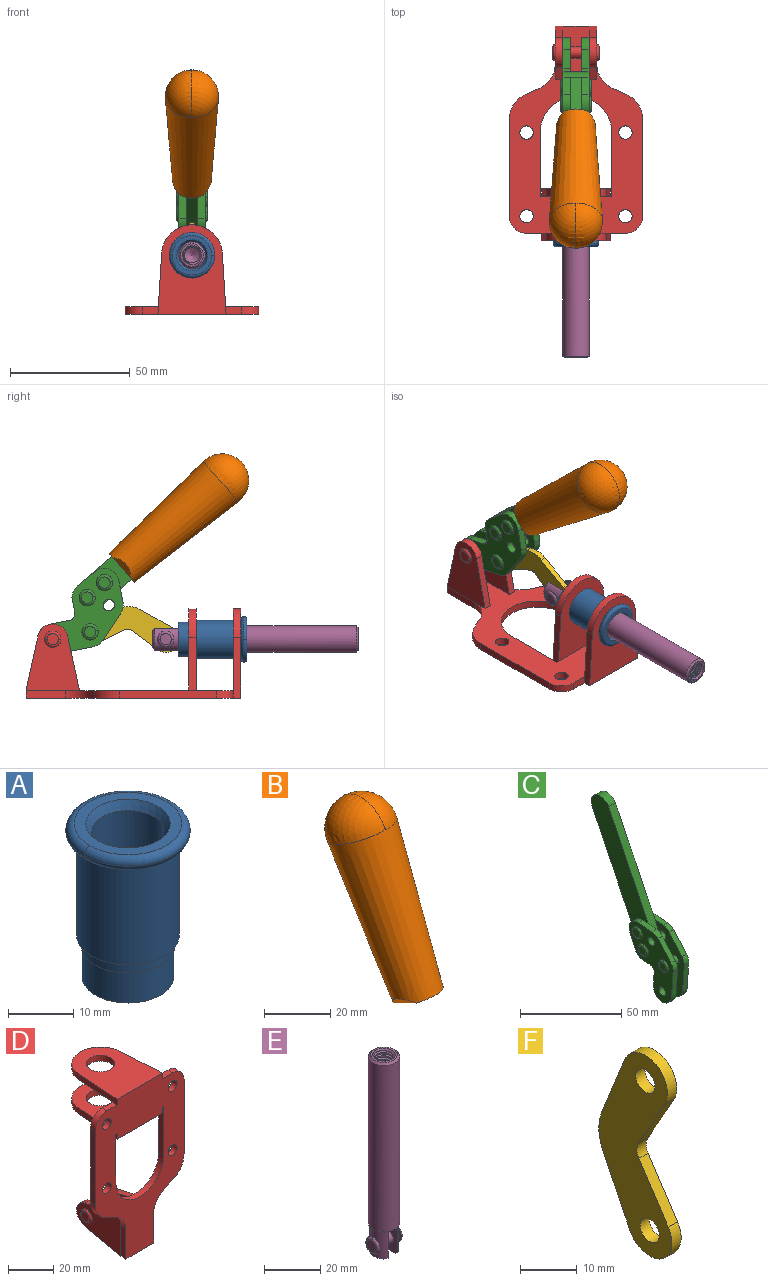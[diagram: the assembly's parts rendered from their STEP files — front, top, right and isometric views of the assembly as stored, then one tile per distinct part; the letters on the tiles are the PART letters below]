
ASSEMBLY  parts=6 mates=6
PART A: 15 faces, bbox 20.6x20.6x28.7 mm
  f0: torus R=8.26mm, axis (0,0,1), area 56.8mm2, adj f1,f10,f12
  f1: torus R=8.26mm, axis (0,0,1), area 56.8mm2, adj f0,f6,f13
  f2: cylinder r=5.59mm len=25.91mm, axis (0,0,1), area 909.6mm2, adj f3,f4
  f3: cone r=6.86mm half-angle=45deg, axis (0,0,-1), area 70.2mm2, adj f2,f14
  f4: cone r=6.47mm half-angle=30deg, axis (0,0,1), area 66.7mm2, adj f2,f13
  f5: cylinder r=7.04mm len=14.07mm, axis (0,0,1), area 252.6mm2, adj f11,f14
  f6: torus R=8.26mm, axis (0,0,1), area 56.8mm2, adj f1,f12,f13
  f7: cylinder r=7.16mm len=14.33mm, axis (0,0,1), area 91.5mm2, adj f9,f11
  f8: cylinder r=7.86mm len=18.42mm, axis (0,0,1), area 909.6mm2, adj f9,f10
  f9: plane 15.72x15.72mm, normal (0,0,-1), area 33mm2, adj f7,f8
  f10: plane 16.51x16.51mm, normal (0,0,-1), area 19.9mm2, adj f0,f8,f12
  f11: plane 14.33x14.33mm, normal (0,0,-1), area 5.7mm2, adj f5,f7
  f12: torus R=8.26mm, axis (0,0,1), area 56.8mm2, adj f0,f6,f10
  f13: plane 16.51x16.51mm, normal (0,0,1), area 82.7mm2, adj f1,f4,f6
  f14: plane 14.07x14.07mm, normal (0,0,-1), area 7.8mm2, adj f3,f5
PART B: 11 faces, bbox 22.3x42.6x64.5 mm
  f0: sphere r=11.13mm, area 411.4mm2, adj f1,f8
  f1: cone r=11.11mm half-angle=3.3deg, axis (0,0.44,0.9), area 3251.8mm2, adj f0,f7,f8,f9,f10
  f2: cylinder r=6.16mm len=11.7mm, axis (1,0,0), area 89.5mm2, adj f3,f4,f5,f6
  f3: plane 60.23x36.75mm, normal (-1,0,0), area 763.6mm2, adj f2,f4,f6,f10
  f4: plane 51.37x25.05mm, normal (0,0.9,-0.44), area 264.2mm2, adj f2,f3,f5,f10
  f5: plane 60.23x36.75mm, normal (1,0,0), area 763.6mm2, adj f2,f4,f6,f10
  f6: plane 51.37x25.05mm, normal (0,-0.9,0.44), area 264.2mm2, adj f2,f3,f5,f10
  f7: plane 9.95x5.95mm, normal (0.71,-0.31,-0.64), area 25.8mm2, adj f1,f10
  f8: sphere r=11.13mm, area 411.4mm2, adj f0,f1
  f9: plane 9.95x5.95mm, normal (-0.71,-0.31,-0.64), area 25.8mm2, adj f1,f10
  f10: plane 14.27x11.38mm, normal (0,-0.44,-0.9), area 106.7mm2, adj f1,f3,f4,f5,f6,f7,f9
PART C: 59 faces, bbox 12.9x60.2x99.6 mm
  f0: torus R=2.39mm, axis (-1,0,0), area 14.9mm2, adj f20,f43,f51
  f1: torus R=2.39mm, axis (-1,0,0), area 14.9mm2, adj f19,f42,f51
  f2: torus R=2.39mm, axis (-1,0,0), area 14.9mm2, adj f18,f35,f51
  f3: torus R=2.39mm, axis (-1,0,0), area 14.9mm2, adj f14,f17,f23
  f4: torus R=2.39mm, axis (-1,0,0), area 14.9mm2, adj f13,f16,f23
  f5: torus R=2.39mm, axis (-1,0,0), area 14.9mm2, adj f12,f15,f23
  f6: cylinder r=2.39mm len=4.78mm, axis (1,0,0), area 46.5mm2, adj f48,f50,f51
  f7: cylinder r=2.39mm len=4.78mm, axis (1,0,0), area 46.5mm2, adj f50,f51
  f8: cylinder r=6.35mm len=12.68mm, axis (1,0,0), area 61.8mm2, adj f38,f39,f50,f51
  f9: cylinder r=2.39mm len=4.78mm, axis (-1,0,0), area 70.5mm2, adj f46,f50
  f10: cylinder r=2.39mm len=4.78mm, axis (-1,0,0), area 46.5mm2, adj f23,f45,f46
  f11: cylinder r=2.39mm len=4.78mm, axis (-1,0,0), area 46.5mm2, adj f23,f46
  f12: plane 4.78x4.78mm, normal (1,0,0), area 17.9mm2, adj f5,f15
  f13: plane 4.78x4.78mm, normal (1,0,0), area 17.9mm2, adj f4,f16
  f14: plane 4.78x4.78mm, normal (1,0,0), area 17.9mm2, adj f3,f17
  f15: torus R=2.39mm, axis (-1,0,0), area 14.9mm2, adj f5,f12,f23
  f16: torus R=2.39mm, axis (-1,0,0), area 14.9mm2, adj f4,f13,f23
  f17: torus R=2.39mm, axis (-1,0,0), area 14.9mm2, adj f3,f14,f23
  f18: plane 4.78x4.78mm, normal (-1,0,0), area 17.9mm2, adj f2,f35
  f19: plane 4.78x4.78mm, normal (-1,0,0), area 17.9mm2, adj f1,f42
  f20: plane 4.78x4.78mm, normal (-1,0,0), area 17.9mm2, adj f0,f43
  f21: plane 2.26x0.2mm, normal (1,0,0), area 0.2mm2, adj f31,f44
  f22: plane 2.26x0.2mm, normal (-1,0,0), area 0.2mm2, adj f41,f44
  f23: plane 39.37x30.77mm, normal (1,0,0), area 565.5mm2, adj f3,f4,f5,f10,f11,f15,f16,f17
  f24: cylinder r=6.1mm len=4.15mm, axis (-1,0,0), area 14.7mm2, adj f23,f25,f32,f46
  f25: plane 10.25x9.01mm, normal (0,-0.75,0.66), area 42.3mm2, adj f23,f24,f26,f46
  f26: cylinder r=6.35mm len=4.64mm, axis (-1,0,0), area 15.6mm2, adj f23,f25,f27,f46
  f27: plane 15.84x3.1mm, normal (0,-1,-0.07), area 49.2mm2, adj f23,f26,f28,f46
  f28: cylinder r=6.35mm len=12.68mm, axis (-1,0,0), area 61.8mm2, adj f23,f27,f29,f46
  f29: plane 8.11x3.1mm, normal (0,1,0.07), area 25.2mm2, adj f23,f28,f30,f46
  f30: cylinder r=3.05mm len=3.25mm, axis (-1,0,0), area 14.8mm2, adj f23,f29,f31,f46
  f31: plane 5.99x3.1mm, normal (0,0.07,-1), area 18.6mm2, adj f21,f23,f30,f44,f46
  f32: plane 9.5x3.1mm, normal (0,-0.07,1), area 29.5mm2, adj f23,f24,f33,f46,f47
  f33: cylinder r=6.1mm len=8.63mm, axis (-1,0,0), area 39.1mm2, adj f23,f32,f34,f47
  f34: plane 8.65x3.96mm, normal (0,0.91,-0.42), area 29.5mm2, adj f23,f33,f44,f47
  f35: torus R=2.39mm, axis (-1,0,0), area 14.9mm2, adj f2,f18,f51
  f36: plane 10.25x9.01mm, normal (0,-0.75,0.66), area 42.3mm2, adj f37,f49,f50,f51
  f37: cylinder r=6.35mm len=4.64mm, axis (1,0,0), area 15.6mm2, adj f36,f38,f50,f51
  f38: plane 15.84x3.1mm, normal (0,-1,-0.07), area 49.2mm2, adj f8,f37,f50,f51
  f39: plane 8.11x3.1mm, normal (0,1,0.07), area 25.2mm2, adj f8,f40,f50,f51
  f40: cylinder r=3.05mm len=3.25mm, axis (1,0,0), area 14.8mm2, adj f39,f41,f50,f51
  f41: plane 5.99x3.1mm, normal (0,0.07,-1), area 18.6mm2, adj f22,f40,f44,f50,f51
  f42: torus R=2.39mm, axis (-1,0,0), area 14.9mm2, adj f1,f19,f51
  f43: torus R=2.39mm, axis (-1,0,0), area 14.9mm2, adj f0,f20,f51
  f44: cylinder r=6.35mm len=12.12mm, axis (-1,0,0), area 128.9mm2, adj f21,f22,f23,f31,f34,f41,f46,f47
  f45: plane 2.65x1.35mm, normal (1,0,0), area 1mm2, adj f10,f55
  f46: plane 39.08x20.42mm, normal (-1,0,0), area 412.5mm2, adj f9,f10,f11,f24,f25,f26,f27,f28
  f47: plane 77.62x39.82mm, normal (1,0,0), area 850mm2, adj f32,f33,f34,f44,f53,f54,f55
  f48: plane 2.65x1.35mm, normal (-1,0,0), area 1mm2, adj f6,f55
  f49: cylinder r=6.1mm len=4.15mm, axis (1,0,0), area 14.7mm2, adj f36,f50,f51,f56
  f50: plane 39.08x20.42mm, normal (1,0,0), area 412.5mm2, adj f6,f7,f8,f9,f36,f37,f38,f39
  f51: plane 39.37x30.77mm, normal (-1,0,0), area 565.5mm2, adj f0,f1,f2,f6,f7,f8,f35,f36
  f52: plane 8.65x3.96mm, normal (0,0.91,-0.42), area 29.5mm2, adj f44,f51,f57,f58
  f53: plane 68.49x33.4mm, normal (0,0.9,-0.44), area 358.1mm2, adj f44,f47,f54,f58
  f54: cylinder r=6.35mm len=12.06mm, axis (1,0,0), area 93.7mm2, adj f47,f53,f55,f58
  f55: plane 68.49x33.4mm, normal (0,-0.9,0.44), area 358.1mm2, adj f44,f45,f46,f47,f48,f50,f54,f58
  f56: plane 9.5x3.1mm, normal (0,-0.07,1), area 29.5mm2, adj f49,f50,f51,f57,f58
  f57: cylinder r=6.1mm len=8.63mm, axis (1,0,0), area 39.1mm2, adj f51,f52,f56,f58
  f58: plane 77.62x39.82mm, normal (-1,0,0), area 850mm2, adj f44,f52,f53,f54,f55,f56,f57
PART D: 55 faces, bbox 55.7x37.4x89.8 mm
  f0: torus R=2.41mm, axis (-1,0,0), area 15mm2, adj f11,f15,f25
  f1: torus R=2.41mm, axis (-1,0,0), area 15mm2, adj f10,f12,f22
  f2: cylinder r=2.78mm len=5.56mm, axis (0,-1,0), area 54.2mm2, adj f30,f54
  f3: cylinder r=14.99mm len=29.97mm, axis (0,-1,0), area 145.9mm2, adj f30,f49,f53,f54
  f4: cylinder r=2.78mm len=5.56mm, axis (0,-1,0), area 54.2mm2, adj f30,f54
  f5: cylinder r=2.78mm len=5.56mm, axis (0,-1,0), area 54.2mm2, adj f30,f54
  f6: cylinder r=2.78mm len=5.56mm, axis (0,-1,0), area 54.2mm2, adj f30,f54
  f7: cylinder r=6.35mm len=12.7mm, axis (0,0,1), area 123.6mm2, adj f27,f51
  f8: cylinder r=6.35mm len=12.7mm, axis (0,0,-1), area 124.7mm2, adj f21,f35
  f9: cylinder r=2.41mm len=11.18mm, axis (-1,0,0), area 169.4mm2, adj f16,f19
  f10: plane 4.83x4.83mm, normal (1,0,0), area 18.3mm2, adj f1,f12
  f11: plane 4.83x4.83mm, normal (-1,0,0), area 18.3mm2, adj f0,f15
  f12: torus R=2.41mm, axis (-1,0,0), area 15mm2, adj f1,f10,f22
  f13: cylinder r=6.35mm len=12.41mm, axis (1,0,0), area 53.4mm2, adj f18,f19,f22,f23
  f14: cylinder r=6.35mm len=12.41mm, axis (-1,0,0), area 53.4mm2, adj f16,f17,f24,f25
  f15: torus R=2.41mm, axis (-1,0,0), area 15mm2, adj f0,f11,f25
  f16: plane 27.86x22.35mm, normal (1,0,0), area 425.4mm2, adj f9,f14,f17,f24,f30
  f17: plane 22.86x4.97mm, normal (0,0.21,0.98), area 72.5mm2, adj f14,f16,f25,f30
  f18: plane 22.86x4.97mm, normal (0,0.21,0.98), area 72.5mm2, adj f13,f19,f22,f30
  f19: plane 27.86x22.35mm, normal (-1,0,0), area 425.4mm2, adj f9,f13,f18,f23,f30
  f20: cylinder r=12.7mm len=25.35mm, axis (0,0,-1), area 119.8mm2, adj f21,f34,f35,f36
  f21: plane 34.21x28.07mm, normal (0,0,-1), area 702.4mm2, adj f8,f20,f30,f34,f36
  f22: plane 27.96x22.45mm, normal (1,0,0), area 407.2mm2, adj f1,f12,f13,f18,f23,f30,f42,f43
  f23: plane 22.86x4.97mm, normal (0,0.21,-0.98), area 72.5mm2, adj f13,f19,f22,f44
  f24: plane 22.86x4.97mm, normal (0,0.21,-0.98), area 72.5mm2, adj f14,f16,f25,f44
  f25: plane 27.86x22.35mm, normal (-1,0,0), area 407.1mm2, adj f0,f14,f15,f17,f24,f30,f45,f46
  f26: plane 3.1x0.95mm, normal (0,0,-1), area 2.7mm2, adj f30,f49,f50,f54
  f27: plane 34.21x28.07mm, normal (0,0,1), area 702.4mm2, adj f7,f28,f30,f50,f52
  f28: cylinder r=12.7mm len=25.35mm, axis (0,0,1), area 118.8mm2, adj f27,f50,f51,f52
  f29: plane 3.1x0.95mm, normal (0,0,-1), area 2.7mm2, adj f30,f52,f53,f54
  f30: plane 86.54x55.63mm, normal (0,1,0), area 2362.9mm2, adj f2,f3,f4,f5,f6,f16,f17,f18
  f31: plane 40.56x3.1mm, normal (-1,0,0), area 125.7mm2, adj f30,f32,f48,f54
  f32: cylinder r=7.11mm len=7.11mm, axis (0,-1,0), area 34.6mm2, adj f30,f31,f33,f54
  f33: plane 6.67x3.1mm, normal (0,0,1), area 20.4mm2, adj f30,f32,f34,f54
  f34: plane 25.39x3.13mm, normal (-1,0.06,0), area 79.5mm2, adj f20,f21,f33,f35,f54
  f35: plane 37.31x28.45mm, normal (0,0,1), area 789.9mm2, adj f8,f20,f34,f36,f54
  f36: plane 25.39x3.13mm, normal (1,0.06,0), area 79.5mm2, adj f20,f21,f35,f37,f54
  f37: plane 6.67x3.1mm, normal (0,0,1), area 20.4mm2, adj f30,f36,f38,f54
  f38: cylinder r=7.11mm len=7.11mm, axis (0,-1,0), area 34.6mm2, adj f30,f37,f39,f54
  f39: plane 40.56x3.1mm, normal (1,0,0), area 125.7mm2, adj f30,f38,f40,f54
  f40: cylinder r=11.18mm len=10.16mm, axis (0,-1,0), area 39.5mm2, adj f30,f39,f41,f54
  f41: plane 6.09x3.1mm, normal (0.42,0,-0.91), area 20.8mm2, adj f30,f40,f42,f54
  f42: cylinder r=11.18mm len=9.41mm, axis (0,-1,0), area 37.2mm2, adj f22,f30,f41,f43,f54
  f43: plane 16.5x3.1mm, normal (1,0,0), area 51.1mm2, adj f22,f42,f44,f54
  f44: plane 17.37x3.1mm, normal (0,0,-1), area 53.8mm2, adj f23,f24,f30,f43,f45,f54
  f45: plane 16.5x3.1mm, normal (-1,0,0), area 51.1mm2, adj f25,f44,f46,f54
  f46: cylinder r=11.18mm len=9.41mm, axis (0,-1,0), area 37.2mm2, adj f25,f30,f45,f47,f54
  f47: plane 6.09x3.1mm, normal (-0.42,0,-0.91), area 20.8mm2, adj f30,f46,f48,f54
  f48: cylinder r=11.18mm len=10.16mm, axis (0,-1,0), area 39.5mm2, adj f30,f31,f47,f54
  f49: plane 26.54x3.1mm, normal (-1,0,0), area 82.3mm2, adj f3,f26,f30,f54
  f50: plane 25.39x3.1mm, normal (1,0.06,0), area 78.8mm2, adj f26,f27,f28,f51,f54
  f51: plane 37.31x28.45mm, normal (0,0,-1), area 789.9mm2, adj f7,f28,f50,f52,f54
  f52: plane 25.39x3.1mm, normal (-1,0.06,0), area 78.8mm2, adj f27,f28,f29,f51,f54
  f53: plane 26.54x3.1mm, normal (1,0,0), area 82.3mm2, adj f3,f29,f30,f54
  f54: plane 89.66x55.63mm, normal (0,-1,0), area 2678.5mm2, adj f2,f3,f4,f5,f6,f26,f29,f31
PART E: 48 faces, bbox 12.6x11.1x86.1 mm
  f0: torus R=2.41mm, axis (-1,0,0), area 15mm2, adj f30,f32,f34
  f1: torus R=2.41mm, axis (-1,0,0), area 15mm2, adj f29,f31,f33
  f2: cylinder r=5.54mm len=72.39mm, axis (0,0,1), area 2518.5mm2, adj f3,f4,f42,f43
  f3: cone r=5.54mm half-angle=45deg, axis (0,0,1), area 7.6mm2, adj f2,f5,f41
  f4: cone r=5.54mm half-angle=45deg, axis (0,0,-1), area 34.9mm2, adj f2,f39
  f5: cylinder r=5.08mm len=11.48mm, axis (0,0,1), area 108.3mm2, adj f3,f7,f8,f41
  f6: cylinder r=2.41mm len=4.83mm, axis (-1,0,0), area 71.2mm2, adj f40,f41
  f7: cylinder r=2.41mm len=4.83mm, axis (-1,0,0), area 7.6mm2, adj f5,f34
  f8: cone r=5.08mm half-angle=45deg, axis (0,0,1), area 10.6mm2, adj f5,f37,f41
  f9: cone r=3.98mm half-angle=45deg, axis (0,0,1), area 17.6mm2, adj f27,f39,f45,f46,f47
  f10: cylinder r=2.41mm len=4.83mm, axis (-1,0,0), area 7.6mm2, adj f33,f38
  f11: cylinder r=3.2mm len=6.4mm, axis (0,0,1), area 78.4mm2, adj f12,f28,f44,f45,f47
  f12: cylinder r=3.2mm len=6.4mm, axis (0,0,1), area 10.5mm2, adj f11,f13,f45,f47
  f13: cylinder r=3.2mm len=6.4mm, axis (0,0,1), area 10.5mm2, adj f12,f14,f45,f47
  f14: cylinder r=3.2mm len=6.4mm, axis (0,0,1), area 10.5mm2, adj f13,f15,f45,f47
  f15: cylinder r=3.2mm len=6.4mm, axis (0,0,1), area 10.5mm2, adj f14,f16,f45,f47
  f16: cylinder r=3.2mm len=6.4mm, axis (0,0,1), area 10.5mm2, adj f15,f17,f45,f47
  f17: cylinder r=3.2mm len=6.4mm, axis (0,0,1), area 10.5mm2, adj f16,f18,f45,f47
  f18: cylinder r=3.2mm len=6.4mm, axis (0,0,1), area 10.5mm2, adj f17,f19,f45,f47
  f19: cylinder r=3.2mm len=6.4mm, axis (0,0,1), area 10.5mm2, adj f18,f20,f45,f47
  f20: cylinder r=3.2mm len=6.4mm, axis (0,0,1), area 10.5mm2, adj f19,f21,f45,f47
  f21: cylinder r=3.2mm len=6.4mm, axis (0,0,1), area 10.5mm2, adj f20,f22,f45,f47
  f22: cylinder r=3.2mm len=6.4mm, axis (0,0,1), area 10.5mm2, adj f21,f23,f45,f47
  f23: cylinder r=3.2mm len=6.4mm, axis (0,0,1), area 10.5mm2, adj f22,f24,f45,f47
  f24: cylinder r=3.2mm len=6.4mm, axis (0,0,1), area 10.5mm2, adj f23,f25,f45,f47
  f25: cylinder r=3.2mm len=6.4mm, axis (0,0,1), area 10.5mm2, adj f24,f26,f45,f47
  f26: cylinder r=3.2mm len=6.4mm, axis (0,0,1), area 10.5mm2, adj f25,f27,f45,f47
  f27: cylinder r=3.2mm len=6.4mm, axis (0,0,1), area 7.4mm2, adj f9,f26,f45,f47
  f28: cone r=3.2mm half-angle=60deg, axis (0,0,1), area 37.2mm2, adj f11
  f29: plane 4.83x4.83mm, normal (-1,0,0), area 18.3mm2, adj f1,f31
  f30: plane 4.83x4.83mm, normal (1,0,0), area 18.3mm2, adj f0,f32
  f31: torus R=2.41mm, axis (-1,0,0), area 15mm2, adj f1,f29,f33
  f32: torus R=2.41mm, axis (-1,0,0), area 15mm2, adj f0,f30,f34
  f33: plane 6.83x6.83mm, normal (1,0,0), area 18.3mm2, adj f1,f10,f31
  f34: plane 6.83x6.83mm, normal (-1,0,0), area 18.3mm2, adj f0,f7,f32
  f35: cone r=5.08mm half-angle=45deg, axis (0,0,1), area 10.6mm2, adj f36,f38,f40
  f36: plane 7.25x1.97mm, normal (0,0,-1), area 10mm2, adj f35,f40
  f37: plane 7.25x1.97mm, normal (0,0,-1), area 10mm2, adj f8,f41
  f38: cylinder r=5.08mm len=11.48mm, axis (0,0,1), area 108.3mm2, adj f10,f35,f40,f42
  f39: plane 9.55x9.55mm, normal (0,0,1), area 22mm2, adj f4,f9
  f40: plane 12.76x10.09mm, normal (1,0,0), area 95.7mm2, adj f6,f35,f36,f38,f42,f43
  f41: plane 12.76x10.09mm, normal (-1,0,0), area 95.7mm2, adj f3,f5,f6,f8,f37,f43
  f42: cone r=5.54mm half-angle=45deg, axis (0,0,1), area 7.6mm2, adj f2,f38,f40
  f43: plane 11.07x4.7mm, normal (0,0,-1), area 50.4mm2, adj f2,f40,f41
  f44: plane 0.89x0.62mm, normal (-1,0,0), area 0.3mm2, adj f11,f45,f46,f47
  f45: bspline ~24.8x7.63mm, area 266.6mm2, adj f9,f11,f12,f13,f14,f15,f16,f17
  f46: bspline ~24.87x7.63mm, area 73.6mm2, adj f9,f44,f45,f47
  f47: bspline ~24.98x7.63mm, area 272.5mm2, adj f9,f11,f12,f13,f14,f15,f16,f17
PART F: 12 faces, bbox 2.3x18.2x42.8 mm
  f0: cylinder r=2.4mm len=4.8mm, axis (1,0,0), area 34.9mm2, adj f4,f11
  f1: cylinder r=10.41mm len=8.47mm, axis (1,0,0), area 20.2mm2, adj f4,f9,f10,f11
  f2: cylinder r=3.05mm len=3.16mm, axis (1,0,0), area 7.7mm2, adj f4,f6,f7,f11
  f3: cylinder r=2.4mm len=4.8mm, axis (1,0,0), area 34.9mm2, adj f4,f11
  f4: plane 42.81x18.23mm, normal (-1,0,0), area 414.1mm2, adj f0,f1,f2,f3,f5,f6,f7,f8
  f5: cylinder r=5.54mm len=10.67mm, axis (1,0,0), area 41.8mm2, adj f4,f6,f10,f11
  f6: plane 11.66x6.53mm, normal (0,-0.87,-0.49), area 30.9mm2, adj f2,f4,f5,f11
  f7: plane 11.17x7.33mm, normal (0,-0.84,0.55), area 30.9mm2, adj f2,f4,f8,f11
  f8: cylinder r=5.54mm len=10.51mm, axis (1,0,0), area 41.8mm2, adj f4,f7,f9,f11
  f9: plane 13.67x6.67mm, normal (0,0.9,-0.44), area 35.1mm2, adj f1,f4,f8,f11
  f10: plane 14.1x5.7mm, normal (0,0.93,0.37), area 35.1mm2, adj f1,f4,f5,f11
  f11: plane 42.81x18.23mm, normal (1,0,0), area 414.1mm2, adj f0,f1,f2,f3,f5,f6,f7,f8
PLACE A rot(axis=(0,-0.71,0.71),180deg) t=(0,9.14,49.23)mm
PLACE B rot(axis=(1,0,0),75deg) t=(-0.04,3.86,9.14)mm
PLACE C rot(axis=(1,0,0),75deg) t=(0,3.86,9.14)mm
PLACE D rot(axis=(1,0,0),90deg) t=(0,9.14,0)mm fixed
PLACE E rot(axis=(1,0,0),90deg) t=(0,9.52,0)mm
PLACE F rot(axis=(0,-0.69,-0.73),180deg) t=(0,11.7,2.14)mm
MATE revolute F.f5 <-> C.f4  axis (-1,0,0) through (0,25.65,27.64)mm
MATE fastened A.f2 <-> D.f7  axis (0,1,0) through (0,-37.25,24.61)mm
MATE revolute D.f0 <-> C.f7  axis (-1,0,0) through (0,41.23,24.61)mm
MATE fastened B.f2 <-> C.f54  axis (1,0,0) through (-2.35,-30.66,91.94)mm
MATE revolute F.f3 <-> E.f6  axis (-1,0,0) through (0,-5.96,24.61)mm
MATE slider E.f2 <-> D.f7  axis (0,-1,0) through (0,-49.26,24.61)mm
